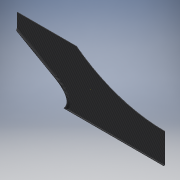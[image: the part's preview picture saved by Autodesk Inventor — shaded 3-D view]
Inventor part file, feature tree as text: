
AUTODESK INVENTOR PART (.ipt)
format: ipt  version: 2018 (Build 220112000, 112)  size: 184,832 bytes
history: native  units: mm
features: extrude x3, other x2, sketch x2, fillet x1, shell x1
ambient origin geometry x8: Origin, YZ Plane, XZ Plane, XY Plane, X Axis, Y Axis, Z Axis, Center Point
bodies: Body1 (feature_tree)
feature tree (9):
  other  "ソリッド1"
  extrude  "押し出し1"  Depth=500.0mm
  other  "作業平面1"
  extrude  "押し出し2"  Depth=200.0mm
  fillet  "フィレット1"  Radius=5.0mm
  shell  "シェル1"  Thickness=150.0deg
  extrude  "押し出し3"  Depth=20.0mm TaperAngle=0.0deg
  sketch  "スケッチ1"
  sketch  "スケッチ3"
